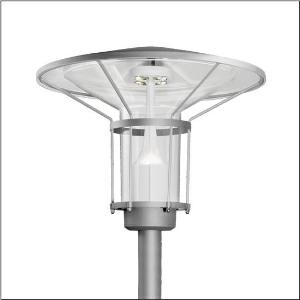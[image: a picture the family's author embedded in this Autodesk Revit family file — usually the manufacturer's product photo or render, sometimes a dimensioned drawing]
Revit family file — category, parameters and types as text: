
# Revit family: laterne_classic_iq___st1_2a_5xa5245kf14h_95b8
name_source: partatom
category: Lighting Fixtures
units: mm (PartAtom-declared; Revit-internal decimal feet)

## family parameters
Cut with Voids When Loaded = No
Host = Face
Light Source = No
Part Type = Normal
Room Calculation Point = No
Round Connector Dimension = Use Diameter
Shared = No

## types (1)
- --- (1 x LED, 1380 lm, 10 W, 4000K)
    Apparent Load = 10 VA
    CIE Flux Codes = 21 60 93 97 100
    Color Rendering = 70
    Color Temperature = 4000K
    Default Elevation = 1800 mm
    Description = Lantern Classic iQ, mast luminaire, Module 540 iQ-SR, primary light control with 3 zone facetted reflector, of plastic, silver coated, highly specular, structured, primary optical cover: cover, of PMMA, transparent, light distribution: ST1.2a, light emission: direct distribution, primary light characteristic: asymmetric, installation type: post-top, LED, High Power LED, rated luminous flux: 1.380lm, luminous efficacy: 138lm/W, light colour: 740, colour temperature: 4000K, control gear: ECG iQ, control: presetting dimming logarithmic, Street-Remote, Auto-Match, Temp-Guard, Lumen-Switch, Night-Set, Smart-Wire, Light-Fading, Desk-Remote (wireless, voltage-free reading and setting of iQ features in the workshop via application-optimized NFC function/RFID function), optimised constant luminous flux control (CLO 2.0), with terminal, 6-pole, max. 2.5mm², mains connection: 230..240V, AC, 50/60Hz, start of lifetime: 10W, end of service life: 10W, reduction: 5W, luminaire housing, upper part, of glass-fibre reinforced polyester, coated, Siteco® metallic grey (DB 702S), diameter: 750mm, height: 596mm, spigot size: d x l = 76 x 70mm (post-top) | with reducer (optional accessory) 60 x 70mm, post-top mast mounting element, of diecast aluminium, coated, Siteco® metallic grey (DB 702S), Module 540 iQ-SR, traffic white (RAL 9016), equipment: standard, protection rating (complete): IP65, insulation class (complete): insulation class II (safety insulation), certification: CE, ENEC, VDE, packaging unit: 1 piece

Light Distribution: ST1.2a
    Height = 596 mm
    Lamp = 1 x LED
    Lamp Light Flux = 1380 lm
    Lamp Power = 10 W
    Lamp count = 1
    Length = 750 mm
    Luminous efficacy = 138 lm/W
    Manufacturer = Siteco
    ModVariant = No
    Model = 5XA5245KF14H
    Number of Poles = 1
    OnlyDefault = Yes
    Power Factor = 1
    Product Name = Laterne Classic iQ | ST1.2a
    Product group = mast luminaire | pylon top
    ProductGroupID = 6100
    Protection Class = Protection class II
    Protection Degree = IP 65
    RLX_Detail_Level = 1
    RLX_Emergency_Light_Flux = 0 lm
    RLX_Emergency_Type = 0
    RLX_Emergency_Type_DB = No
    RlxData = <blob elided: 95793 chars, md5=f227373b>
    Socket = socket
    Standby Power = 0 W
    System Light Flux = 1380 lm
    System Power = 10 W
    Type Comments = factory setting: luminous flux: 100 % | dim-lin: 254 | 401 mA
    Type Image = l_1006052.jpg
    URL = http://relux.com
    VarID = @adj_110519
    Voltage = 0 V
    Weight = 0.00 kg
    Width = 0 mm  [stored 0 ft]

note: [stored X ft] marks values corroborated as IEEE doubles in the binary element streams (Revit-internal decimal feet)

## geometry (parser evidence)
native form markers: Blend x4, Sweep x11
no freeform markers — native parametric forms only
